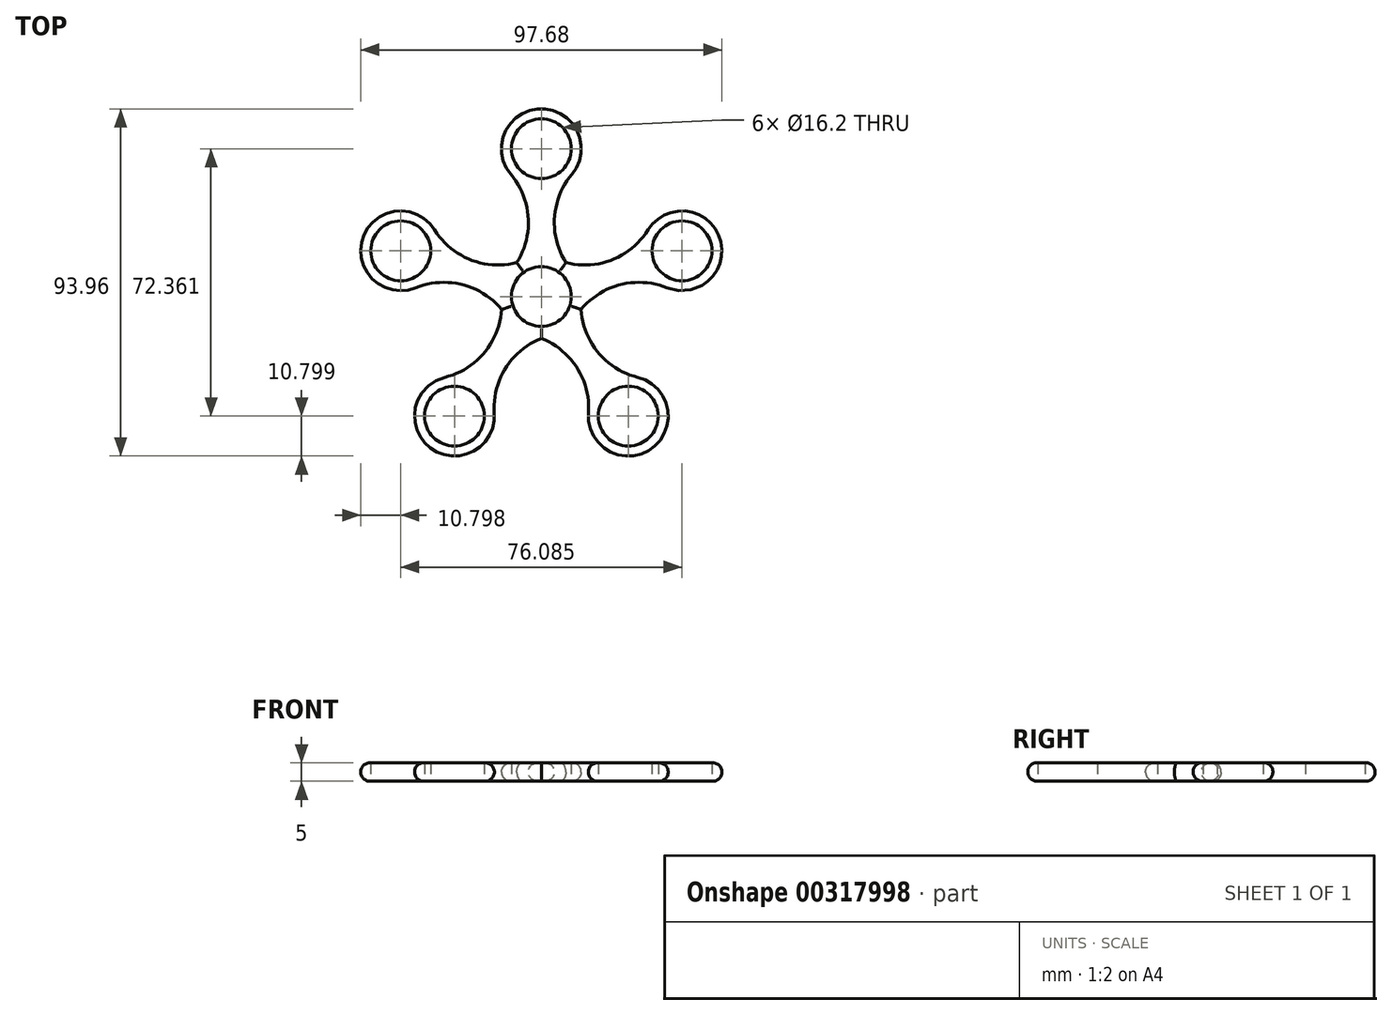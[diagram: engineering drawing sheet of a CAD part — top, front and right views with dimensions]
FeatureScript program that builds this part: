
annotation { "Feature Type Name" : "Feature", "Feature Type Description" : "" }
export const myFeature = defineFeature(function(context is Context, id is Id, definition is map)
    precondition{}
    {
        {
            var Q0;
            Q0=qCreatedBy(makeId("Top.planeOp"),FACE);
            var sketch = newSketch(context, id + "F0", { "sketchPlane" : qUnion([Q0])});
            skCircle(sketch, "E0", {"center": v(0, 0) * mm, "radius": 10.8 * mm, "construction": true});
            skLineSegment(sketch, "E1.anchor1", {"start": v(0, 0) * mm, "end": v(0, 40) * mm, "construction": true});
            skArc(sketch, "E2", {"start": v(8.26, 33.04) * mm, "mid": v(0, 50.8) * mm, "end": v(-8.26, 33.04) * mm});
            skLineSegment(sketch, "E3", {"start": v(-3.5, 20) * mm, "end": v(3.5, 20) * mm, "construction": true});
            skPoint(sketch, "E4", {"position": v(0, 20) * mm});
            skArc(sketch, "E5", {"start": v(-8.26, 6.96) * mm, "mid": v(-3.5, 20) * mm, "end": v(-8.26, 33.04) * mm});
            skPoint(sketch, "E5.second.point", {"position": v(-8.26, 33.04) * mm});
            skPoint(sketch, "E5.third.point", {"position": v(-8.26, 6.96) * mm});
            skArc(sketch, "E6.MirrorCS", {"start": v(8.26, 6.96) * mm, "mid": v(3.5, 20) * mm, "end": v(8.26, 33.04) * mm});
            skArc(sketch, "E7.1.0", {"start": v(-28.87, 18.07) * mm, "mid": v(-48.31, 15.7) * mm, "end": v(-33.98, 2.35) * mm});
            skArc(sketch, "E7.1.1", {"start": v(-9.17, -5.7) * mm, "mid": v(-20.1, 2.85) * mm, "end": v(-33.98, 2.35) * mm});
            skArc(sketch, "E7.1.2", {"start": v(-4.06, 10) * mm, "mid": v(-17.94, 9.5) * mm, "end": v(-28.87, 18.07) * mm});
            skArc(sketch, "E7.2.0", {"start": v(-26.1, -21.88) * mm, "mid": v(-29.86, -41.1) * mm, "end": v(-12.74, -31.59) * mm});
            skArc(sketch, "E7.2.1", {"start": v(2.6, -10.48) * mm, "mid": v(-8.92, -18.24) * mm, "end": v(-12.74, -31.59) * mm});
            skArc(sketch, "E7.2.2", {"start": v(-10.77, -0.77) * mm, "mid": v(-14.59, -14.12) * mm, "end": v(-26.1, -21.88) * mm});
            skArc(sketch, "E7.3.0", {"start": v(12.74, -31.59) * mm, "mid": v(29.86, -41.1) * mm, "end": v(26.1, -21.88) * mm});
            skArc(sketch, "E7.3.1", {"start": v(10.77, -0.77) * mm, "mid": v(14.59, -14.12) * mm, "end": v(26.1, -21.88) * mm});
            skArc(sketch, "E7.3.2", {"start": v(-2.6, -10.48) * mm, "mid": v(8.92, -18.24) * mm, "end": v(12.74, -31.59) * mm});
            skArc(sketch, "E7.4.0", {"start": v(33.98, 2.35) * mm, "mid": v(48.31, 15.7) * mm, "end": v(28.87, 18.07) * mm});
            skArc(sketch, "E7.4.1", {"start": v(4.06, 10) * mm, "mid": v(17.94, 9.5) * mm, "end": v(28.87, 18.07) * mm});
            skArc(sketch, "E7.4.2", {"start": v(9.17, -5.7) * mm, "mid": v(20.1, 2.85) * mm, "end": v(33.98, 2.35) * mm});
            skSolve(sketch);
        }
        {
            var Q0;
            Q0=qSketchRegion(id+"F0",true);
            extrude(context, id + "F1", {"entities" : qUnion([Q0]), "depth" : 5 * mm});
        }
        {
            var Q0;
            Q0=sQuery(id+"F0.wireOp",VERTEX,"E7.1.0.center");
            var Q1;
            Q1=sQuery(id+"F0.wireOp",VERTEX,"E7.2.0.center");
            var Q2;
            Q2=sQuery(id+"F0.wireOp",VERTEX,"E7.3.0.center");
            var Q3;
            Q3=sQuery(id+"F0.wireOp",VERTEX,"E0.center");
            var Q4;
            Q4=sQuery(id+"F0.wireOp",VERTEX,"E7.4.0.center");
            var Q5;
            Q5=sQuery(id+"F0.wireOp",VERTEX,"E1.anchor1.end");
            var Q6;
            Q6=makeQuery(id+"F1.opExtrude","SWEPT_BODY",BODY,{"disambiguationData":[OSD([sQuery(id+"F0.wireOp",EDGE,"E2"),sQuery(id+"F0.wireOp",EDGE,"E5"),sQuery(id+"F0.wireOp",EDGE,"E6.MirrorCS"),sQuery(id+"F0.wireOp",EDGE,"E7.1.0"),sQuery(id+"F0.wireOp",EDGE,"E7.1.1"),sQuery(id+"F0.wireOp",EDGE,"E7.1.2"),sQuery(id+"F0.wireOp",EDGE,"E7.2.0"),sQuery(id+"F0.wireOp",EDGE,"E7.2.1"),sQuery(id+"F0.wireOp",EDGE,"E7.2.2"),sQuery(id+"F0.wireOp",EDGE,"E7.3.0"),sQuery(id+"F0.wireOp",EDGE,"E7.3.1"),sQuery(id+"F0.wireOp",EDGE,"E7.3.2"),sQuery(id+"F0.wireOp",EDGE,"E7.4.0"),sQuery(id+"F0.wireOp",EDGE,"E7.4.1"),sQuery(id+"F0.wireOp",EDGE,"E7.4.2")])]});
            hole(context, id + "F2", {"style" : HoleStyle.SIMPLE, "endStyle" : HoleEndStyle.THROUGH, "oppositeDirection" : true, "holeDiameter" : 16.2 * mm, "tappedDepth" : 12 * mm, "tapClearance" : 3, "locations" : qUnion([Q0, Q1, Q2, Q3, Q4, Q5]), "scope" : qUnion([Q6])});
        }
        {
            var Q0;
            Q0=makeQuery(id+"F1.opExtrude","CAP_EDGE",EDGE,{"disambiguationData":[OSD([sQuery(id+"F0.wireOp",EDGE,"E7.1.0")])],"isStart":false});
            var Q1;
            Q1=makeQuery(id+"F1.opExtrude","CAP_EDGE",EDGE,{"disambiguationData":[OSD([sQuery(id+"F0.wireOp",EDGE,"E7.1.0")])],"isStart":true});
            var Q2;
            Q2=makeQuery(id+"F1.opExtrude","CAP_EDGE",EDGE,{"disambiguationData":[OSD([sQuery(id+"F0.wireOp",EDGE,"E5")])],"isStart":false});
            var Q3;
            Q3=makeQuery(id+"F1.opExtrude","CAP_EDGE",EDGE,{"disambiguationData":[OSD([sQuery(id+"F0.wireOp",EDGE,"E2")])],"isStart":false});
            var Q4;
            Q4=makeQuery(id+"F1.opExtrude","CAP_EDGE",EDGE,{"disambiguationData":[OSD([sQuery(id+"F0.wireOp",EDGE,"E7.4.1")])],"isStart":false});
            var Q5;
            Q5=makeQuery(id+"F1.opExtrude","CAP_EDGE",EDGE,{"disambiguationData":[OSD([sQuery(id+"F0.wireOp",EDGE,"E7.4.0")])],"isStart":false});
            var Q6;
            Q6=makeQuery(id+"F1.opExtrude","CAP_EDGE",EDGE,{"disambiguationData":[OSD([sQuery(id+"F0.wireOp",EDGE,"E7.3.1")])],"isStart":false});
            var Q7;
            Q7=makeQuery(id+"F1.opExtrude","CAP_EDGE",EDGE,{"disambiguationData":[OSD([sQuery(id+"F0.wireOp",EDGE,"E7.2.1")])],"isStart":false});
            var Q8;
            Q8=makeQuery(id+"F1.opExtrude","CAP_EDGE",EDGE,{"disambiguationData":[OSD([sQuery(id+"F0.wireOp",EDGE,"E7.2.2")])],"isStart":true});
            var Q9;
            Q9=makeQuery(id+"F1.opExtrude","CAP_EDGE",EDGE,{"disambiguationData":[OSD([sQuery(id+"F0.wireOp",EDGE,"E7.3.2")])],"isStart":true});
            var Q10;
            Q10=makeQuery(id+"F1.opExtrude","CAP_EDGE",EDGE,{"disambiguationData":[OSD([sQuery(id+"F0.wireOp",EDGE,"E7.4.2")])],"isStart":true});
            var Q11;
            Q11=makeQuery(id+"F1.opExtrude","CAP_EDGE",EDGE,{"disambiguationData":[OSD([sQuery(id+"F0.wireOp",EDGE,"E5")])],"isStart":true});
            fillet(context, id + "F3", {"entities" : qUnion([Q0, Q1, Q2, Q3, Q4, Q5, Q6, Q7, Q8, Q9, Q10, Q11]), "radius" : 2.5 * mm, "tangentPropagation" : true, "allowEdgeOverflow" : false});
        }
    });
